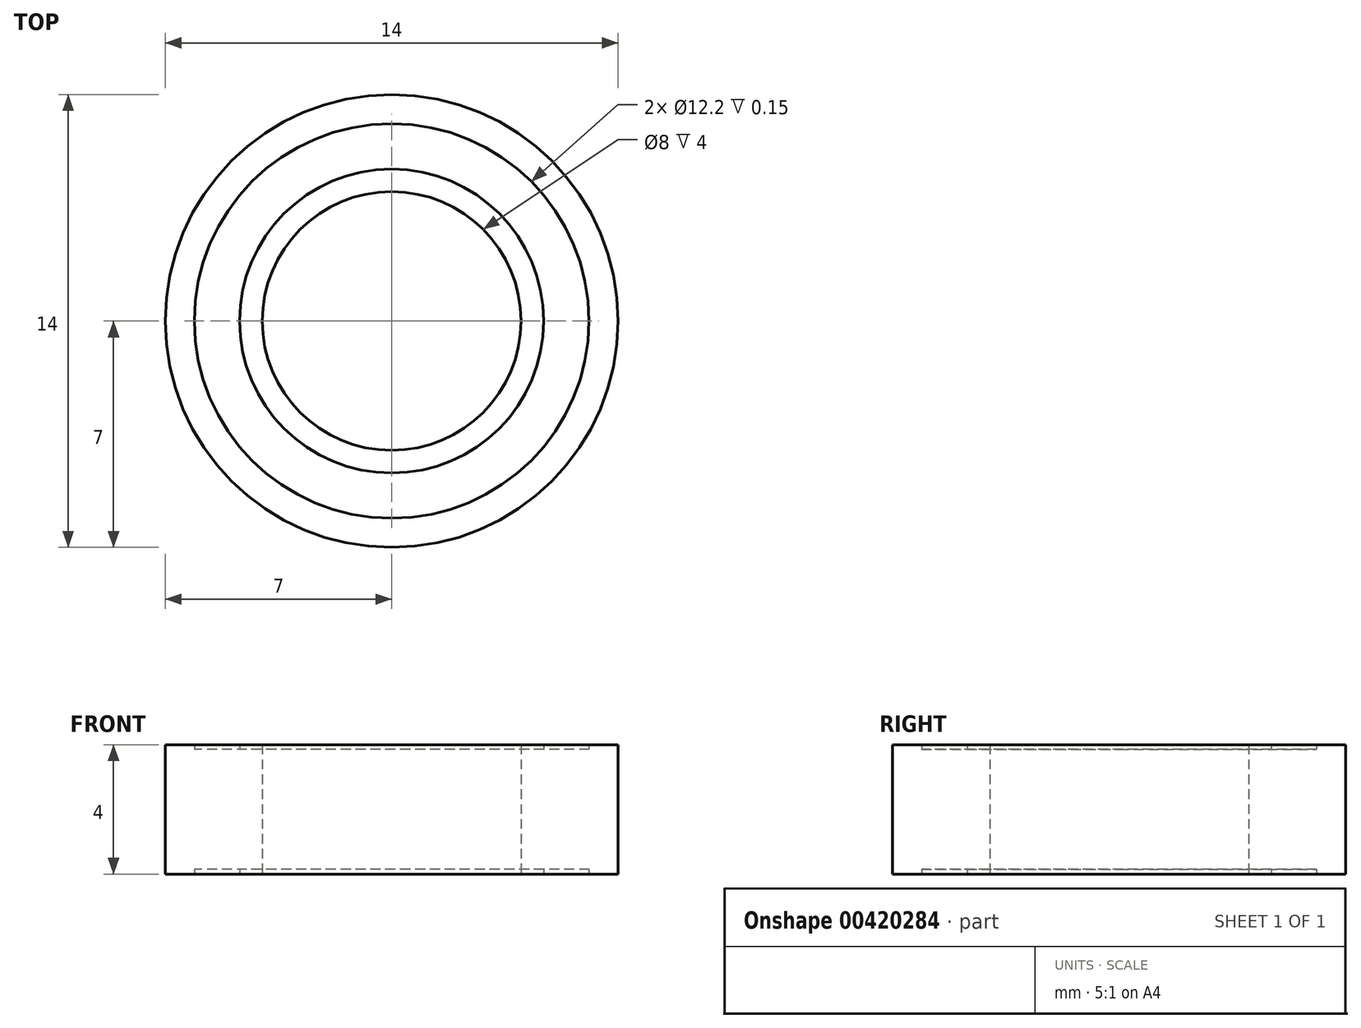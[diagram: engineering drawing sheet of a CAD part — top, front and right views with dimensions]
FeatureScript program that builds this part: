
annotation { "Feature Type Name" : "Feature", "Feature Type Description" : "" }
export const myFeature = defineFeature(function(context is Context, id is Id, definition is map)
    precondition{}
    {
        {
            var Q0;
            Q0=qCreatedBy(makeId("Top.planeOp"),FACE);
            var sketch = newSketch(context, id + "F0", { "sketchPlane" : qUnion([Q0])});
            skCircle(sketch, "E0", {"center": v(0, 0) * mm, "radius": 7 * mm});
            skCircle(sketch, "E1", {"center": v(0, 0) * mm, "radius": 4 * mm});
            skCircle(sketch, "E2.0", {"center": v(0, 0) * mm, "radius": 6.1 * mm});
            skCircle(sketch, "E3.0", {"center": v(0, 0) * mm, "radius": 4.7 * mm});
            skSolve(sketch);
        }
        {
            var Q0;
            Q0=makeQuery(id+"F0.imprint","IMPRINT",FACE,{"disambiguationData":[TD([[makeQuery(id+"F0.imprint","IMPRINT",EDGE,{"derivedFrom":sQuery(id+"F0.wireOp",EDGE,"E2.0")}),1.0]])]});
            extrude(context, id + "F1", {"entities" : qUnion([Q0]), "endBound" : BoundingType.SYMMETRIC, "depth" : (4 - 0.3) * mm});
        }
        {
            var Q0;
            Q0=makeQuery(id+"F0.imprint","IMPRINT",FACE,{"disambiguationData":[TD([[makeQuery(id+"F0.imprint","IMPRINT",EDGE,{"derivedFrom":sQuery(id+"F0.wireOp",EDGE,"E0")}),1.0]])]});
            var Q1;
            Q1=makeQuery(id+"F0.imprint","IMPRINT",FACE,{"disambiguationData":[TD([[makeQuery(id+"F0.imprint","IMPRINT",EDGE,{"derivedFrom":sQuery(id+"F0.wireOp",EDGE,"E1")}),-1.0]])]});
            extrude(context, id + "F2", {"entities" : qUnion([Q0, Q1]), "operationType" : NewBodyOperationType.ADD, "endBound" : BoundingType.SYMMETRIC, "depth" : 4 * mm});
        }
    });
